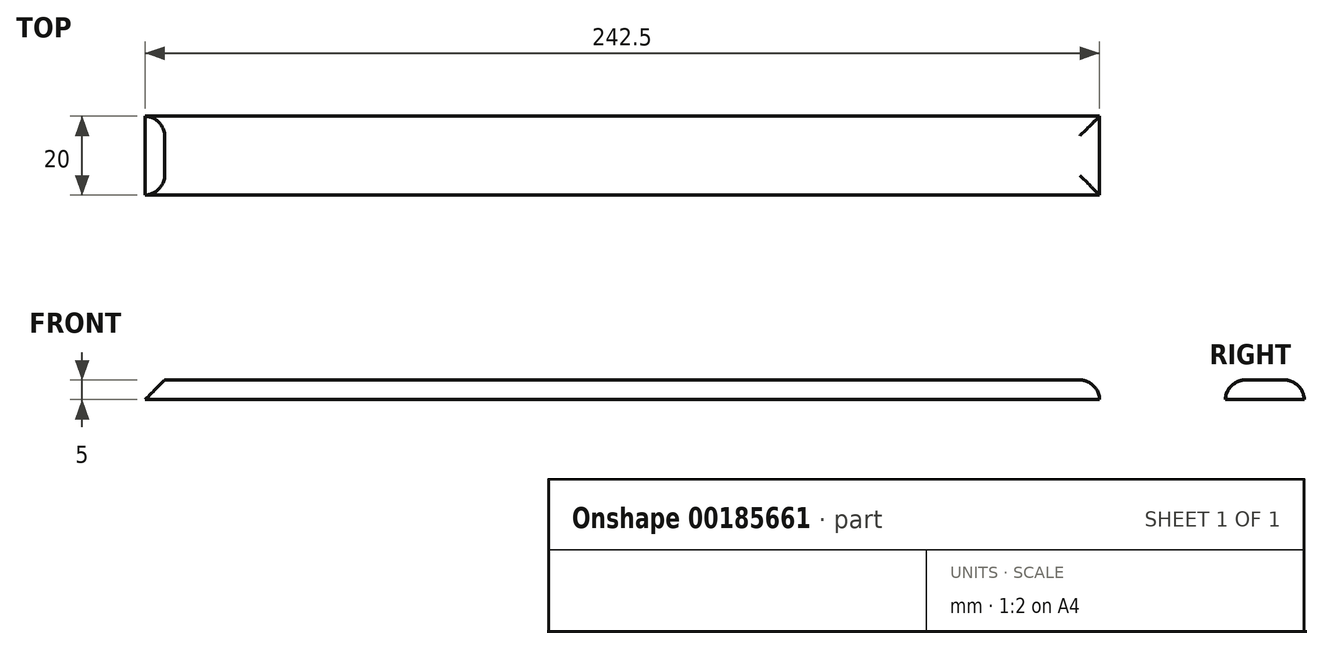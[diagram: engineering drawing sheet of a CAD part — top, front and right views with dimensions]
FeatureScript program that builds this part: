
annotation { "Feature Type Name" : "Feature", "Feature Type Description" : "" }
export const myFeature = defineFeature(function(context is Context, id is Id, definition is map)
    precondition{}
    {
        {
            var Q0;
            Q0=qCreatedBy(makeId("Top.planeOp"),FACE);
            var sketch = newSketch(context, id + "F0", { "sketchPlane" : qUnion([Q0])});
            skLineSegment(sketch, "E0.bottom", {"start": v(-125, 10) * mm, "end": v(125, 10) * mm});
            skLineSegment(sketch, "E0.top", {"start": v(-125, -10) * mm, "end": v(125, -10) * mm});
            skLineSegment(sketch, "E0.left", {"start": v(-125, 10) * mm, "end": v(-125, -10) * mm});
            skLineSegment(sketch, "E0.right", {"start": v(125, 10) * mm, "end": v(125, -10) * mm});
            skPoint(sketch, "E0.middle", {"position": v(0, 0) * mm});
            skLineSegment(sketch, "E1", {"start": v(-125, 0) * mm, "end": v(125, 0) * mm});
            skSolve(sketch);
        }
        {
            var Q0;
            {var subQ0=sQuery(id+"F0.wireOp",EDGE,"E0.bottom");Q0=makeQuery(id+"F0.imprint","IMPRINT",FACE,{"disambiguationData":[TD([[makeQuery(id+"F0.imprint","IMPRINT",EDGE,{"derivedFrom":subQ0}),-1.0]])]});}
            var Q1;
            {var subQ0=sQuery(id+"F0.wireOp",EDGE,"E0.top");Q1=makeQuery(id+"F0.imprint","IMPRINT",FACE,{"disambiguationData":[TD([[makeQuery(id+"F0.imprint","IMPRINT",EDGE,{"derivedFrom":subQ0}),1.0]])]});}
            extrude(context, id + "F1", {"entities" : qUnion([Q0, Q1]), "depth" : 5 * mm});
        }
        {
            var Q0;
            Q0=makeQuery(id+"F1.opExtrude","CAP_EDGE",EDGE,{"disambiguationData":[OSD([sQuery(id+"F0.wireOp",EDGE,"E0.left")])],"isStart":false});
            chamfer(context, id + "F2", {"entities" : qUnion([Q0]), "width" : 12.5 * mm, "tangentPropagation" : true});
        }
        {
            var Q0;
            Q0=makeQuery(id+"F1.opExtrude","CAP_EDGE",EDGE,{"disambiguationData":[OSD([sQuery(id+"F0.wireOp",EDGE,"E0.bottom")])],"isStart":false});
            var Q1;
            Q1=makeQuery(id+"F1.opExtrude","CAP_EDGE",EDGE,{"disambiguationData":[OSD([sQuery(id+"F0.wireOp",EDGE,"E0.top")])],"isStart":false});
            var Q2;
            Q2=makeQuery(id+"F1.opExtrude","CAP_EDGE",EDGE,{"disambiguationData":[OSD([sQuery(id+"F0.wireOp",EDGE,"E0.right")])],"isStart":false});
            fillet(context, id + "F3", {"entities" : qUnion([Q0, Q1, Q2]), "radius" : 5 * mm, "rho" : .4, "crossSection" : FilletCrossSection.CONIC, "allowEdgeOverflow" : false});
        }
    });
